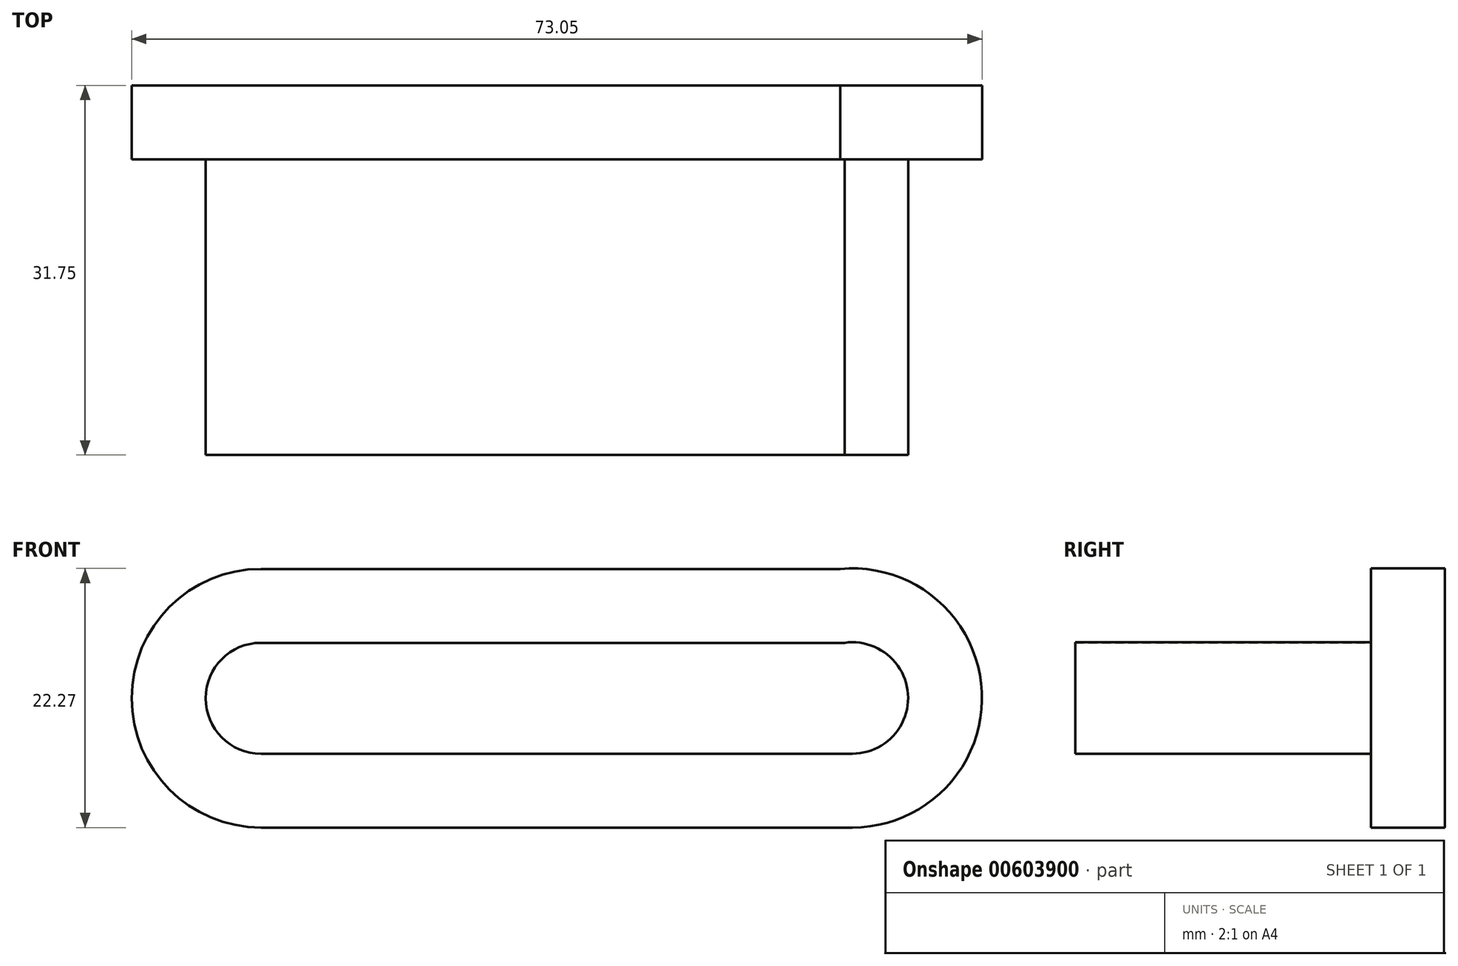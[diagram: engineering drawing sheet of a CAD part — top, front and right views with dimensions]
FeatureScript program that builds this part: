
annotation { "Feature Type Name" : "Feature", "Feature Type Description" : "" }
export const myFeature = defineFeature(function(context is Context, id is Id, definition is map)
    precondition{}
    {
        {
            var Q0;
            Q0=qCreatedBy(makeId("Front.planeOp"),FACE);
            var sketch = newSketch(context, id + "F0", { "sketchPlane" : qUnion([Q0])});
            skLineSegment(sketch, "E0", {"start": v(0, 0) * mm, "end": v(50.8, 0) * mm});
            skLineSegment(sketch, "E1", {"start": v(0, 9.53) * mm, "end": v(50.13, 9.53) * mm});
            skArc(sketch, "E2", {"start": v(0, 9.53) * mm, "mid": v(-4.76, 4.76) * mm, "end": v(0, 0) * mm});
            skArc(sketch, "E3", {"start": v(50.8, 0) * mm, "mid": v(55.57, 5.12) * mm, "end": v(50.13, 9.52) * mm});
            skLineSegment(sketch, "E4.0", {"start": v(0, -6.35) * mm, "end": v(50.8, -6.35) * mm});
            skArc(sketch, "E4.1", {"start": v(0, 15.88) * mm, "mid": v(-11.11, 4.76) * mm, "end": v(0, -6.35) * mm});
            skLineSegment(sketch, "E4.2", {"start": v(0, 15.88) * mm, "end": v(49.77, 15.88) * mm});
            skArc(sketch, "E4.3", {"start": v(50.8, -6.35) * mm, "mid": v(61.92, 5.3) * mm, "end": v(49.77, 15.88) * mm});
            skSolve(sketch);
        }
        {
            var Q0;
            Q0=makeQuery(id+"F0.imprint","IMPRINT",FACE,{"disambiguationData":[TD([[makeQuery(id+"F0.imprint","IMPRINT",EDGE,{"derivedFrom":sQuery(id+"F0.wireOp",EDGE,"E0")}),1.0]])]});
            extrude(context, id + "F1", {"entities" : qUnion([Q0]), "depth" : 25.4 * mm, "offsetDistance" : 25.4 * mm});
        }
        {
            var Q0;
            Q0=makeQuery(id+"F0.imprint","IMPRINT",FACE,{"disambiguationData":[TD([[makeQuery(id+"F0.imprint","IMPRINT",EDGE,{"derivedFrom":sQuery(id+"F0.wireOp",EDGE,"E0")}),-1.0]])]});
            var Q1;
            Q1=makeQuery(id+"F0.imprint","IMPRINT",FACE,{"disambiguationData":[TD([[makeQuery(id+"F0.imprint","IMPRINT",EDGE,{"derivedFrom":sQuery(id+"F0.wireOp",EDGE,"E0")}),1.0]])]});
            extrude(context, id + "F2", {"entities" : qUnion([Q0, Q1]), "operationType" : NewBodyOperationType.REMOVE, "oppositeDirection" : true, "depth" : 6.35 * mm, "offsetDistance" : 25.4 * mm});
        }
        {
            var Q0;
            Q0=makeQuery(id+"F0.imprint","IMPRINT",FACE,{"disambiguationData":[TD([[makeQuery(id+"F0.imprint","IMPRINT",EDGE,{"derivedFrom":sQuery(id+"F0.wireOp",EDGE,"E0")}),-1.0]])]});
            var Q1;
            Q1=makeQuery(id+"F0.imprint","IMPRINT",FACE,{"disambiguationData":[TD([[makeQuery(id+"F0.imprint","IMPRINT",EDGE,{"derivedFrom":sQuery(id+"F0.wireOp",EDGE,"E0")}),1.0]])]});
            var Q2;
            Q2=sQuery(id+"F0.wireOp",EDGE,"E4.3");
            var Q3;
            Q3=sQuery(id+"F0.wireOp",EDGE,"E4.2");
            var Q4;
            Q4=sQuery(id+"F0.wireOp",EDGE,"E4.1");
            var Q5;
            Q5=sQuery(id+"F0.wireOp",EDGE,"E4.0");
            extrude(context, id + "F3", {"entities" : qUnion([Q0, Q1]), "operationType" : NewBodyOperationType.ADD, "surfaceEntities" : qUnion([Q2, Q3, Q4, Q5]), "oppositeDirection" : true, "depth" : 6.35 * mm, "offsetDistance" : 25.4 * mm});
        }
    });
